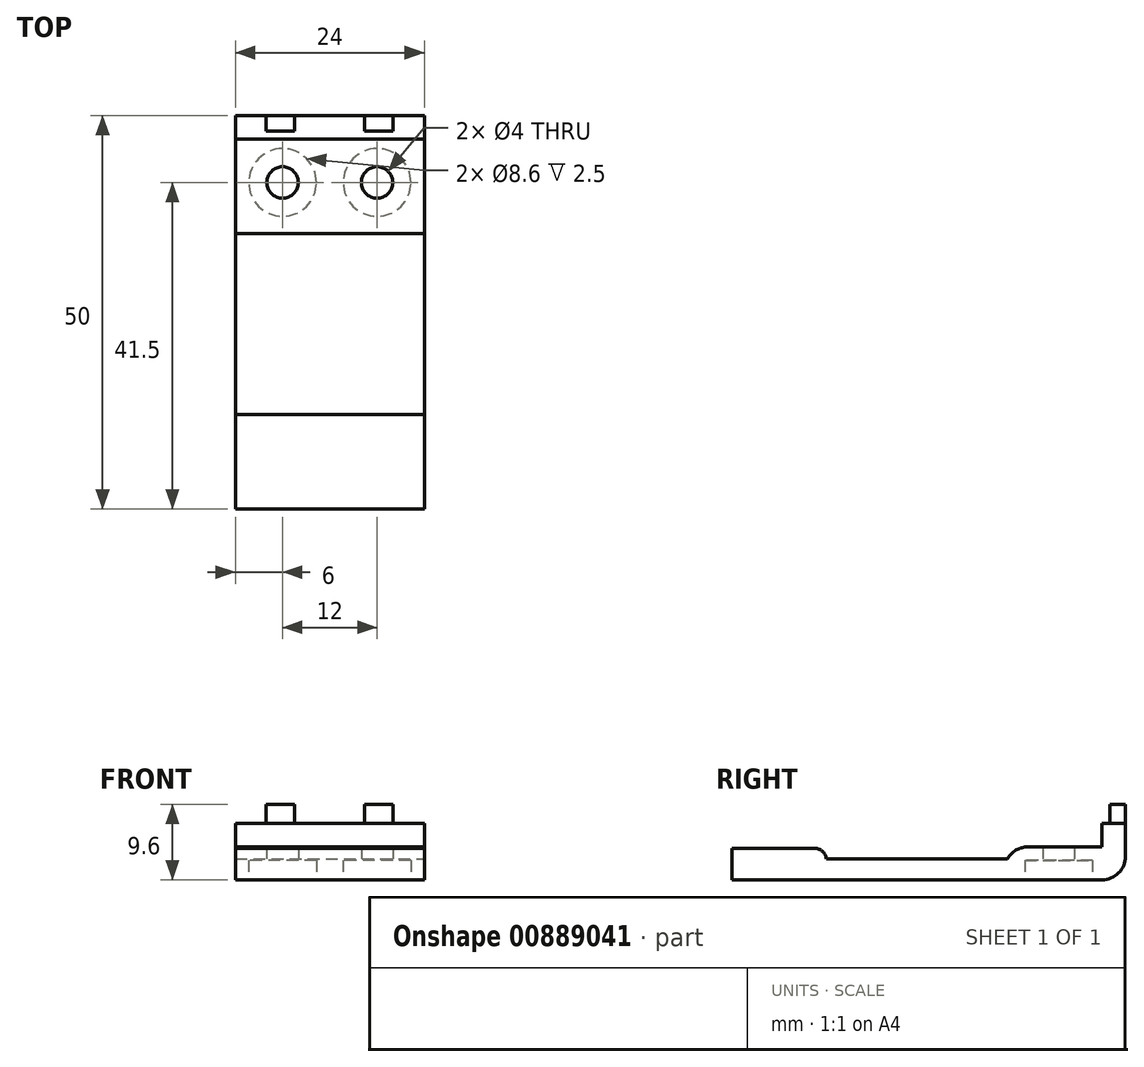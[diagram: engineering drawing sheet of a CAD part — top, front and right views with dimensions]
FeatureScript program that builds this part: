
annotation { "Feature Type Name" : "Feature", "Feature Type Description" : "" }
export const myFeature = defineFeature(function(context is Context, id is Id, definition is map)
    precondition{}
    {
        {
            var Q0;
            Q0=qCreatedBy(makeId("Top.planeOp"),FACE);
            var sketch = newSketch(context, id + "F0", { "sketchPlane" : qUnion([Q0])});
            skLineSegment(sketch, "E0.top", {"start": v(0, -50) * mm, "end": v(24, -50) * mm});
            skLineSegment(sketch, "E0.left", {"start": v(0, 0) * mm, "end": v(0, -50) * mm});
            skLineSegment(sketch, "E0.right", {"start": v(24, 0) * mm, "end": v(24, -50) * mm});
            skLineSegment(sketch, "E1.bottom", {"start": v(0, 0) * mm, "end": v(24, 0) * mm});
            skLineSegment(sketch, "E1.top", {"start": v(0, -3) * mm, "end": v(24, -3) * mm});
            skLineSegment(sketch, "E1.left", {"start": v(0, 0) * mm, "end": v(0, -3) * mm});
            skLineSegment(sketch, "E1.right", {"start": v(24, 0) * mm, "end": v(24, -3) * mm});
            skLineSegment(sketch, "E2.top", {"start": v(0, -15) * mm, "end": v(24, -15) * mm});
            skLineSegment(sketch, "E2.left", {"start": v(0, -3) * mm, "end": v(0, -15) * mm});
            skLineSegment(sketch, "E2.right", {"start": v(24, -3) * mm, "end": v(24, -15) * mm});
            skCircle(sketch, "E3", {"center": v(6, -8.5) * mm, "radius": 2 * mm});
            skCircle(sketch, "E4", {"center": v(18, -8.5) * mm, "radius": 2 * mm});
            skCircle(sketch, "E5", {"center": v(6, -8.5) * mm, "radius": 4.3 * mm});
            skCircle(sketch, "E6", {"center": v(18, -8.5) * mm, "radius": 4.3 * mm});
            skLineSegment(sketch, "E7.left", {"start": v(0, -50) * mm, "end": v(0, -50) * mm});
            skLineSegment(sketch, "E7.right", {"start": v(24, -50) * mm, "end": v(24, -50) * mm});
            skLineSegment(sketch, "E8.bottom", {"start": v(24, -38) * mm, "end": v(0, -38) * mm});
            skLineSegment(sketch, "E8.top", {"start": v(24, -50) * mm, "end": v(0, -50) * mm});
            skLineSegment(sketch, "E8.left", {"start": v(24, -38) * mm, "end": v(24, -50) * mm});
            skLineSegment(sketch, "E8.right", {"start": v(0, -38) * mm, "end": v(0, -50) * mm});
            skSolve(sketch);
        }
        {
            var Q0;
            Q0 = qSketchRegion(id + "F0", true);
            extrude(context, id + "F1", {"entities" : qUnion([Q0]), "depth" : 2.7 * mm, "offsetDistance" : 25 * mm});
        }
        {
            var Q0;
            Q0=makeQuery(id+"F0.imprint","IMPRINT",FACE,{"disambiguationData":[TD([[makeQuery(id+"F0.imprint","IMPRINT",EDGE,{"derivedFrom":sQuery(id+"F0.wireOp",EDGE,"E1.bottom")}),-1.0]])]});
            var Q1;
            Q1=makeQuery(id+"F0.imprint","IMPRINT",FACE,{"disambiguationData":[TD([[makeQuery(id+"F0.imprint","IMPRINT",EDGE,{"derivedFrom":sQuery(id+"F0.wireOp",EDGE,"E1.top")}),-1.0]])]});
            var Q2;
            Q2=makeQuery(id+"F0.imprint","IMPRINT",FACE,{"disambiguationData":[TD([[makeQuery(id+"F0.imprint","IMPRINT",EDGE,{"derivedFrom":sQuery(id+"F0.wireOp",EDGE,"E3")}),-1.0]])]});
            var Q3;
            Q3=makeQuery(id+"F0.imprint","IMPRINT",FACE,{"disambiguationData":[TD([[makeQuery(id+"F0.imprint","IMPRINT",EDGE,{"derivedFrom":sQuery(id+"F0.wireOp",EDGE,"E4")}),-1.0]])]});
            extrude(context, id + "F2", {"entities" : qUnion([Q0, Q1, Q2, Q3]), "operationType" : NewBodyOperationType.ADD, "depth" : 4.2 * mm, "offsetDistance" : 25 * mm});
        }
        {
            var Q0;
            Q0=makeQuery(id+"F0.imprint","IMPRINT",FACE,{"disambiguationData":[TD([[makeQuery(id+"F0.imprint","IMPRINT",EDGE,{"derivedFrom":sQuery(id+"F0.wireOp",EDGE,"E3")}),-1.0]])]});
            var Q1;
            Q1=makeQuery(id+"F0.imprint","IMPRINT",FACE,{"disambiguationData":[TD([[makeQuery(id+"F0.imprint","IMPRINT",EDGE,{"derivedFrom":sQuery(id+"F0.wireOp",EDGE,"E4")}),-1.0]])]});
            extrude(context, id + "F3", {"entities" : qUnion([Q0, Q1]), "operationType" : NewBodyOperationType.REMOVE, "depth" : 2.5 * mm, "offsetDistance" : 25 * mm});
        }
        {
            var Q0;
            Q0=makeQuery(id+"F0.imprint","IMPRINT",FACE,{"disambiguationData":[TD([[makeQuery(id+"F0.imprint","IMPRINT",EDGE,{"derivedFrom":sQuery(id+"F0.wireOp",EDGE,"E1.bottom")}),-1.0]])]});
            extrude(context, id + "F4", {"entities" : qUnion([Q0]), "operationType" : NewBodyOperationType.ADD, "depth" : 7.2 * mm, "offsetDistance" : 25 * mm});
        }
        {
            var Q0;
            Q0=makeQuery(id+"F4.opExtrude","CAP_FACE",FACE,{"disambiguationData":[OSD([sQuery(id+"F0.wireOp",EDGE,"E1.bottom"),sQuery(id+"F0.wireOp",EDGE,"E1.left"),sQuery(id+"F0.wireOp",EDGE,"E1.right"),sQuery(id+"F0.wireOp",EDGE,"E1.top")])],"isStart":false});
            var sketch = newSketch(context, id + "F5", { "sketchPlane" : qUnion([Q0])});
            skLineSegment(sketch, "E9", {"start": v(0, 0) * mm, "end": v(3.9, 0) * mm});
            skLineSegment(sketch, "E10", {"start": v(3.9, 0) * mm, "end": v(7.5, 0) * mm});
            skLineSegment(sketch, "E11", {"start": v(7.5, 0) * mm, "end": v(16.1, 0) * mm});
            skLineSegment(sketch, "E12", {"start": v(16.2, 0) * mm, "end": v(20, 0) * mm});
            skLineSegment(sketch, "E13", {"start": v(20, 0) * mm, "end": v(24, 0) * mm});
            skLineSegment(sketch, "E14", {"start": v(3.9, 0) * mm, "end": v(3.9, -2) * mm});
            skLineSegment(sketch, "E15", {"start": v(3.9, -2) * mm, "end": v(7.5, -2) * mm});
            skLineSegment(sketch, "E16", {"start": v(16.4, 0) * mm, "end": v(16.4, -2) * mm});
            skLineSegment(sketch, "E17", {"start": v(16.4, -2) * mm, "end": v(20, -2) * mm});
            skLineSegment(sketch, "E18", {"start": v(20, -2) * mm, "end": v(20, 0) * mm});
            skLineSegment(sketch, "E19", {"start": v(7.5, -2) * mm, "end": v(7.5, 0) * mm});
            skLineSegment(sketch, "E20", {"start": v(20, 0) * mm, "end": v(16.2, 0) * mm});
            skLineSegment(sketch, "E21", {"start": v(7.5, 0) * mm, "end": v(3.9, 0) * mm});
            skSolve(sketch);
        }
        {
            var Q0;
            Q0 = qSketchRegion(id + "F5", true);
            extrude(context, id + "F6", {"entities" : qUnion([Q0]), "operationType" : NewBodyOperationType.ADD, "depth" : 2.4 * mm, "offsetDistance" : 25 * mm});
        }
        {
            var Q0;
            Q0=makeQuery(id+"F1.opExtrude","CAP_EDGE",EDGE,{"disambiguationData":[OSD([sQuery(id+"F0.wireOp",EDGE,"E1.bottom")])],"isStart":true});
            var Q1;
            Q1=makeQuery(id+"F1.opExtrude","SWEPT_EDGE",EDGE,{"disambiguationData":[OSD([sQuery(id+"F0.wireOp",EDGE,"E0.top"),sQuery(id+"F0.wireOp",EDGE,"E0.right")])]});
            var Q2;
            Q2=makeQuery(id+"F1.opExtrude","SWEPT_EDGE",EDGE,{"disambiguationData":[OSD([sQuery(id+"F0.wireOp",EDGE,"E0.top"),sQuery(id+"F0.wireOp",EDGE,"E0.left")])]});
            var Q3;
            Q3=makeQuery(id+"F2.opExtrude","CAP_EDGE",EDGE,{"disambiguationData":[OSD([sQuery(id+"F0.wireOp",EDGE,"E2.top")])],"isStart":false});
            fillet(context, id + "F7", {"entities" : qUnion([Q0, Q1, Q2, Q3]), "radius" : 3 * mm, "tangentPropagation" : true, "allowEdgeOverflow" : false});
        }
        {
            var Q0;
            Q0=makeQuery(id+"F0.imprint","IMPRINT",FACE,{"disambiguationData":[TD([[makeQuery(id+"F0.imprint","IMPRINT",EDGE,{"derivedFrom":sQuery(id+"F0.wireOp",EDGE,"E8.bottom")}),1.0]])]});
            extrude(context, id + "F8", {"entities" : qUnion([Q0]), "operationType" : NewBodyOperationType.ADD, "depth" : 4 * mm, "offsetDistance" : 25 * mm});
        }
        {
            var Q0;
            Q0=makeQuery(id+"F8.opExtrude","CAP_EDGE",EDGE,{"disambiguationData":[OSD([sQuery(id+"F0.wireOp",EDGE,"E8.bottom")])],"isStart":false});
            var Q1;
            Q1=makeQuery(id+"F8.opExtrude","CAP_EDGE",EDGE,{"disambiguationData":[OSD([sQuery(id+"F0.wireOp",EDGE,"E8.top")])],"isStart":false});
            fillet(context, id + "F9", {"entities" : qUnion([Q0, Q1]), "radius" : 1.5 * mm, "tangentPropagation" : true, "allowEdgeOverflow" : false});
        }
    });
